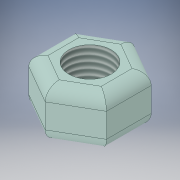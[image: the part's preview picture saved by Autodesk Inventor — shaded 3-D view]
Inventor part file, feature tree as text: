
AUTODESK INVENTOR PART (.ipt)
format: ipt  version: 2019 (Build 230136000, 136)  size: 140,288 bytes
history: native  units: mm
features: other x1, extrude x1, fillet x1, thread x1, sketch x1
ambient origin geometry x8: Origin, YZ Plane, XZ Plane, XY Plane, X Axis, Y Axis, Z Axis, Center Point
bodies: Body1 (feature_tree)
feature tree (5):
  other  "Sólido1"
  extrude  "Extrusión1"  TaperAngle=0.0deg  [1 undecoded]
  fillet  "Empalme1"  Radius=7.0mm
  thread  "Rosca1"  [1 undecoded]
  sketch  "Boceto1"  dims[d0=6.4mm d1=0.0mm d2=7.0mm d3=8.0mm d4=0.0mm d5=2.0mm d6=10.0mm d7=0.0mm]
note: 2 required parameter values undecoded (feature->parameter linkage not recoverable at this tier; creation-order binding heuristic only, values carry confidence <= 0.55)
